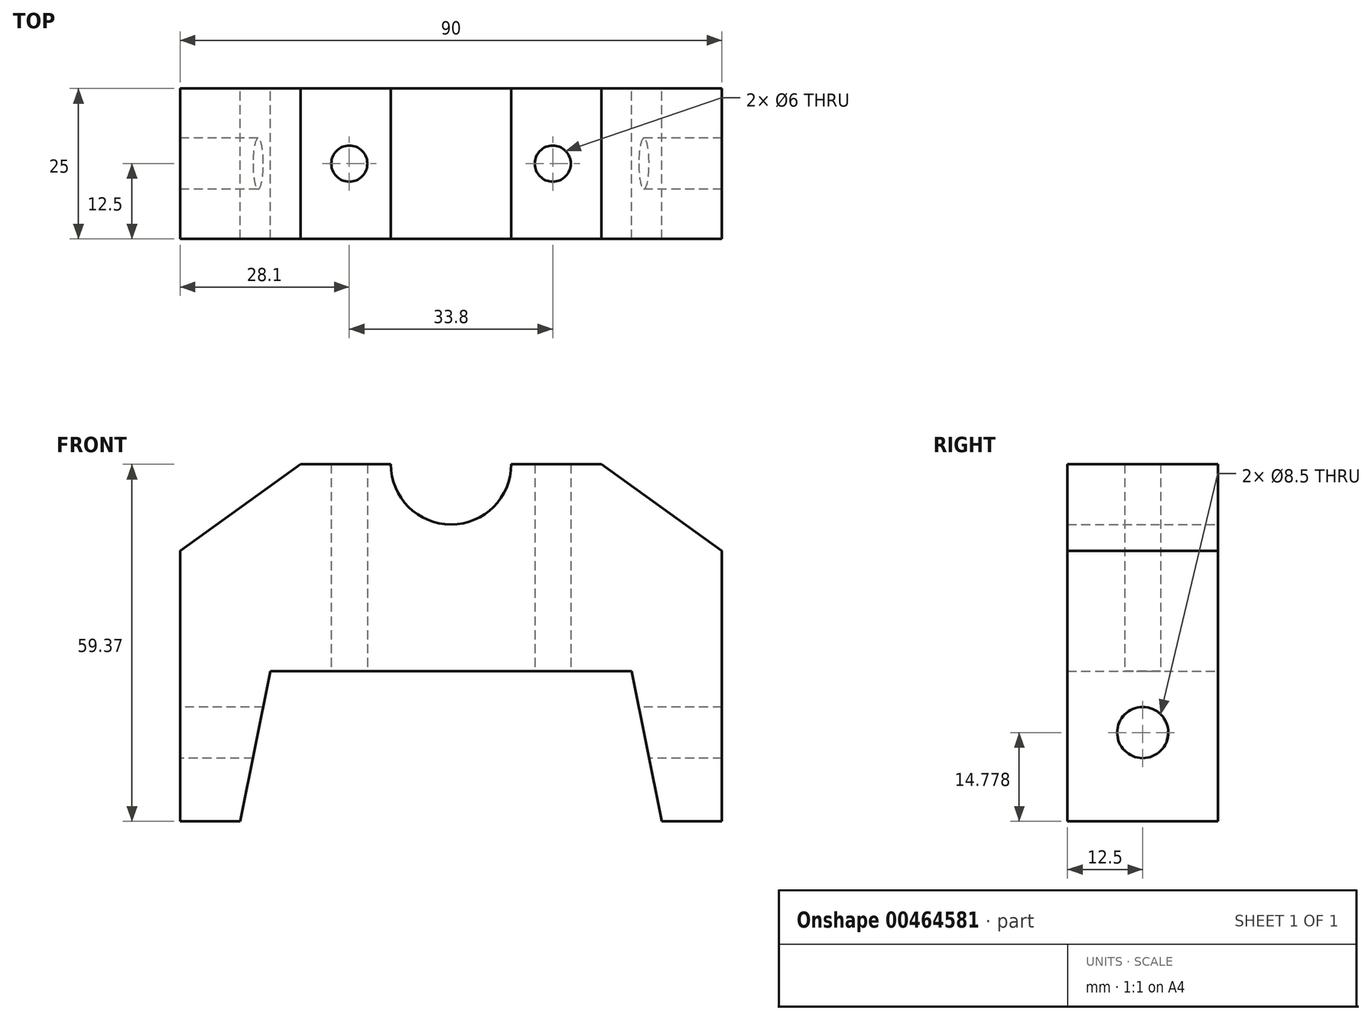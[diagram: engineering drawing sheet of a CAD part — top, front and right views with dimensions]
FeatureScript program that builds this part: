
annotation { "Feature Type Name" : "Feature", "Feature Type Description" : "" }
export const myFeature = defineFeature(function(context is Context, id is Id, definition is map)
    precondition{}
    {
        {
            var Q0;
            Q0=qCreatedBy(makeId("Front.planeOp"),FACE);
            var sketch = newSketch(context, id + "F0", { "sketchPlane" : qUnion([Q0])});
            skLineSegment(sketch, "E0", {"start": v(0, 0) * mm, "end": v(45, 0) * mm, "construction": true});
            skLineSegment(sketch, "E1", {"start": v(0, 0) * mm, "end": v(0, 19.37) * mm, "construction": true});
            skLineSegment(sketch, "E2", {"start": v(0, 0) * mm, "end": v(-45, 0) * mm, "construction": true});
            skLineSegment(sketch, "E3", {"start": v(0, 0) * mm, "end": v(0, -15) * mm, "construction": true});
            skLineSegment(sketch, "E4", {"start": v(-45, 5) * mm, "end": v(-45, 0) * mm});
            skLineSegment(sketch, "E5", {"start": v(-45, 0) * mm, "end": v(-45, -40) * mm});
            skLineSegment(sketch, "E6", {"start": v(45, 0) * mm, "end": v(45, -40) * mm});
            skLineSegment(sketch, "E7", {"start": v(45, 0) * mm, "end": v(45, 5) * mm});
            skArc(sketch, "E8", {"start": v(-10, 19.37) * mm, "mid": v(0, 9.37) * mm, "end": v(10, 19.37) * mm});
            skLineSegment(sketch, "E9", {"start": v(-45, -40) * mm, "end": v(-35, -40) * mm});
            skLineSegment(sketch, "E10", {"start": v(45, -40) * mm, "end": v(35, -40) * mm});
            skLineSegment(sketch, "E11", {"start": v(0, -15) * mm, "end": v(-30, -15) * mm});
            skLineSegment(sketch, "E12", {"start": v(0, -15) * mm, "end": v(30, -15) * mm});
            skLineSegment(sketch, "E13", {"start": v(-35, -40) * mm, "end": v(-30, -15) * mm});
            skLineSegment(sketch, "E14", {"start": v(30, -15) * mm, "end": v(35, -40) * mm});
            skLineSegment(sketch, "E15", {"start": v(-10, 19.37) * mm, "end": v(-25, 19.37) * mm});
            skLineSegment(sketch, "E16", {"start": v(-25, 19.37) * mm, "end": v(-45, 5) * mm});
            skLineSegment(sketch, "E17", {"start": v(10, 19.37) * mm, "end": v(25, 19.37) * mm});
            skLineSegment(sketch, "E18", {"start": v(25, 19.37) * mm, "end": v(45, 5) * mm});
            skSolve(sketch);
        }
        {
            var Q0;
            Q0 = qSketchRegion(id + "F0", true);
            extrude(context, id + "F1", {"entities" : qUnion([Q0]), "depth" : 25 * mm, "offsetDistance" : 25 * mm});
        }
        {
            var Q0;
            Q0=makeQuery(id+"F1.opExtrude","SWEPT_FACE",FACE,{"disambiguationData":[OSD([sQuery(id+"F0.wireOp",EDGE,"E11"),sQuery(id+"F0.wireOp",EDGE,"E12")])]});
            var sketch = newSketch(context, id + "F2", { "sketchPlane" : qUnion([Q0])});
            skCircle(sketch, "E19", {"center": v(-16.9, 12.5) * mm, "radius": 3 * mm});
            skLineSegment(sketch, "E20", {"start": v(-16.9, 12.5) * mm, "end": v(16.9, 12.5) * mm, "construction": true});
            skCircle(sketch, "E21", {"center": v(16.9, 12.5) * mm, "radius": 3 * mm});
            skSolve(sketch);
        }
        {
            var Q0;
            Q0 = qSketchRegion(id + "F2", true);
            extrude(context, id + "F3", {"entities" : qUnion([Q0]), "operationType" : NewBodyOperationType.REMOVE, "endBound" : BoundingType.THROUGH_ALL, "oppositeDirection" : true, "depth" : 25 * mm, "offsetDistance" : 25 * mm});
        }
        {
            var Q0;
            Q0=makeQuery(id+"F1.opExtrude","SWEPT_FACE",FACE,{"disambiguationData":[OSD([sQuery(id+"F0.wireOp",EDGE,"E4"),sQuery(id+"F0.wireOp",EDGE,"E5")])]});
            var sketch = newSketch(context, id + "F4", { "sketchPlane" : qUnion([Q0])});
            skCircle(sketch, "E22", {"center": v(12.5, -25.22) * mm, "radius": 4.25 * mm});
            skSolve(sketch);
        }
        {
            var Q0;
            Q0 = qSketchRegion(id + "F4", true);
            extrude(context, id + "F5", {"entities" : qUnion([Q0]), "operationType" : NewBodyOperationType.REMOVE, "endBound" : BoundingType.THROUGH_ALL, "oppositeDirection" : true, "depth" : 25 * mm, "offsetDistance" : 25 * mm});
        }
    });
